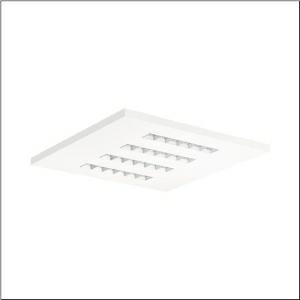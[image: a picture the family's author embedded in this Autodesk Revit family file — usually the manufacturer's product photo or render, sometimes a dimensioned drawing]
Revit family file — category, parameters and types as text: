
# Revit family: silica_21_square_51mx6mds44w
name_source: partatom
category: Lighting Fixtures
units: mm (PartAtom-declared; Revit-internal decimal feet)

## family parameters
Cut with Voids When Loaded = No
Host = Face
Light Source = No
Part Type = Normal
Room Calculation Point = No
Round Connector Dimension = Use Diameter
Shared = No

## types (1)
- --- (1 x LED, 4600 lm, 27.2 W, 4000K)
    Apparent Load = 27 VA
    CIE Flux Codes = 83 98 100 100 100
    Color Rendering = 80
    Color Temperature = 4000K
    Default Elevation = 1800 mm
    Description = Silica 21 Square, office luminaire, primary light control with lens, of PMMA, primary anti-glare with reflector, of PC, white, CAT 2 (L<= 3000cd/m²), light emission: direct distribution, primary light characteristic: symmetric, installation type: lay-in mounting, LED, rated luminous flux: 4.600lm, luminous efficacy: 169lm/W, light colour: 840, colour temperature: 4000K, control gear: DALI 2, with terminal, 5-pole, mains connection: 220..240V, AC, 50/60Hz, rated input power: 27.2W, luminaire housing, of sheet steel, coated, traffic white (RAL 9016), module: M600, length: 597mm, width: 597mm, height: 33mm, protection rating (complete): IP20, insulation class (complete): insulation class I (protective earthing), certification: CE, ENEC, VDE, permissible operating ambient temperature: -20..+40°C, standard: EN 50419, packaging unit: 1 piece
    Height = 0 mm  [stored 0 ft]
    Lamp = 1 x LED
    Lamp Light Flux = 4600 lm
    Lamp Power = 27.2 W
    Lamp count = 1
    Length = 597 mm
    Luminous efficacy = 169 lm/W
    Manufacturer = Siteco
    ModVariant = No
    Model = 51MX6MDS44W
    Mounting Place = Ceiling
    Mounting Type = Recessed
    Number of Poles = 1
    OnlyDefault = Yes
    Power Factor = 1
    Product Name = Silica 21 Square
    Product group = office luminaire | ceiling recessed
    ProductGroupID = 400
    Protection Class = Protection class I
    Protection Degree = IP 20
    RLX_Detail_Level = 1
    RLX_Emergency_Light_Flux = 0 lm
    RLX_Emergency_Type = 0
    RLX_Emergency_Type_DB = No
    RlxData = <blob elided: 18621 chars, md5=7de512c5>
    Socket = socket
    Standby Power = 0 W
    System Light Flux = 4600 lm
    System Power = 27 W
    Type Comments = factory setting: luminous flux: 100 % | dim-lin: 254 | 366 mA
    Type Image = l_1275220.jpg
    URL = http://relux.com
    VarID = @adj_088827
    Voltage = 0 V
    Weight = 0.00 kg
    Width = 597 mm

note: [stored X ft] marks values corroborated as IEEE doubles in the binary element streams (Revit-internal decimal feet)

## geometry (parser evidence)
native form markers: Blend x4, Sweep x11
no freeform markers — native parametric forms only
